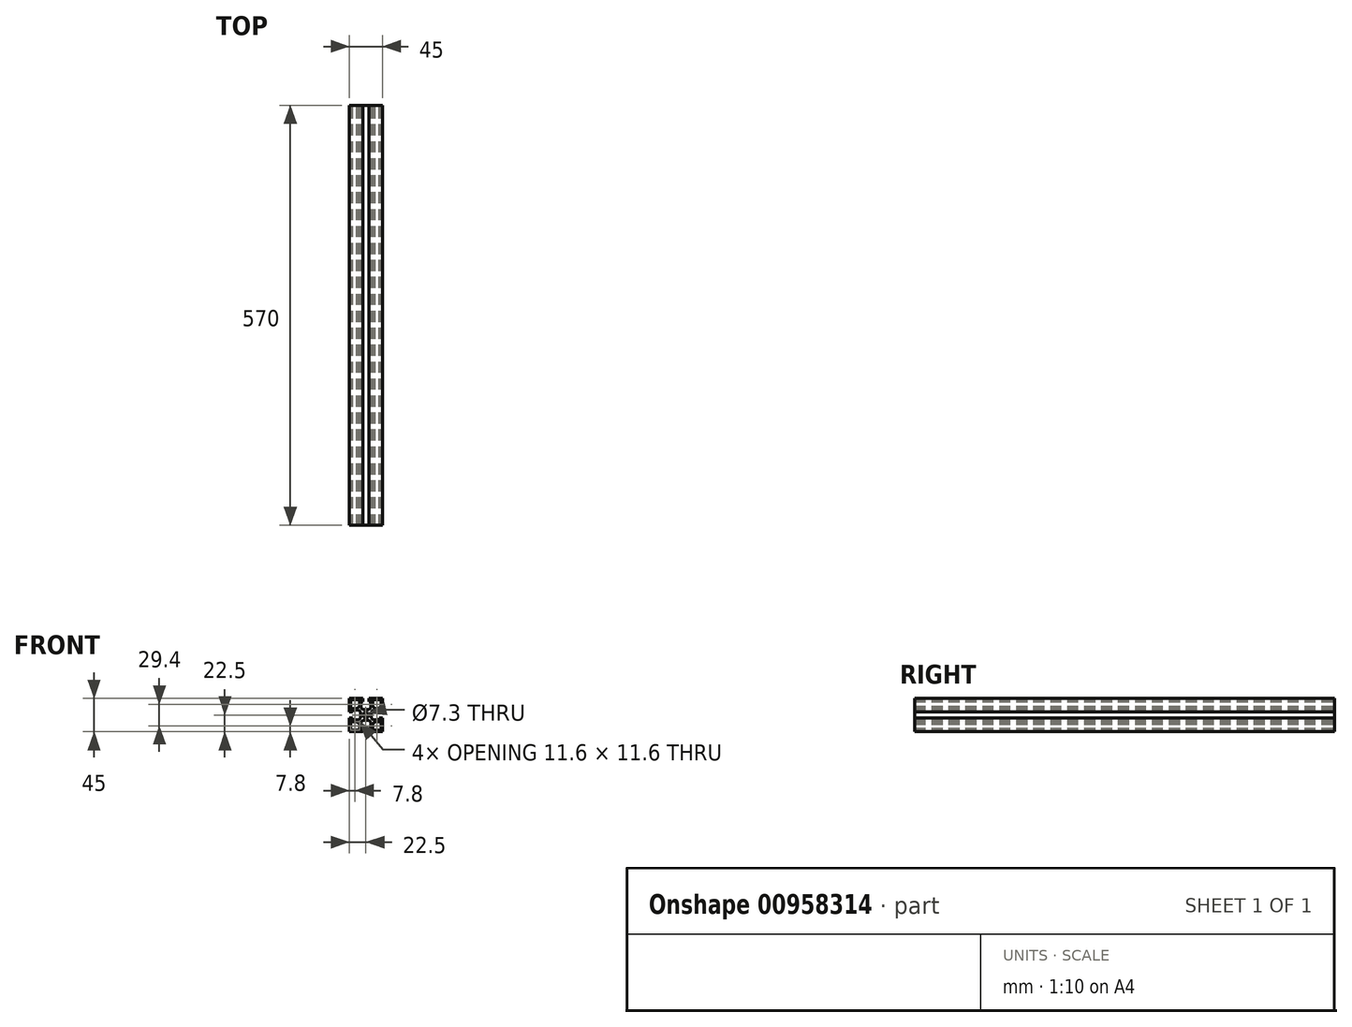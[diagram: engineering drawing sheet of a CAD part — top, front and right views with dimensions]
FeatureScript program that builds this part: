
annotation { "Feature Type Name" : "Feature", "Feature Type Description" : "" }
export const myFeature = defineFeature(function(context is Context, id is Id, definition is map)
    precondition{}
    {
        {
            var Q0;
            Q0=qCreatedBy(makeId("Front.planeOp"),FACE);
            var sketch = newSketch(context, id + "F0", { "sketchPlane" : qUnion([Q0])});
            skLineSegment(sketch, "E0", {"start": v(-22.5, 22.5) * mm, "end": v(-4.15, 22.5) * mm});
            skLineSegment(sketch, "E1", {"start": v(-4.15, 22.5) * mm, "end": v(-4.15, 18) * mm});
            skLineSegment(sketch, "E2", {"start": v(-4.15, 18) * mm, "end": v(-5.75, 18) * mm});
            skArc(sketch, "E3", {"start": v(-5.75, 18) * mm, "mid": v(-6.25, 18.5) * mm, "end": v(-6.75, 18) * mm});
            skLineSegment(sketch, "E4", {"start": v(-6.75, 18) * mm, "end": v(-6.75, 9.8) * mm});
            skLineSegment(sketch, "E5", {"start": v(-6.75, 9.8) * mm, "end": v(-4.15, 7.2) * mm});
            skLineSegment(sketch, "E6", {"start": v(-4.15, 7.2) * mm, "end": v(4.15, 7.2) * mm});
            skLineSegment(sketch, "E7", {"start": v(4.15, 7.2) * mm, "end": v(6.75, 9.8) * mm});
            skLineSegment(sketch, "E8", {"start": v(6.75, 9.8) * mm, "end": v(6.75, 18) * mm});
            skArc(sketch, "E9", {"start": v(6.75, 18) * mm, "mid": v(6.25, 18.5) * mm, "end": v(5.75, 18) * mm});
            skLineSegment(sketch, "E10", {"start": v(5.75, 18) * mm, "end": v(4.15, 18) * mm});
            skLineSegment(sketch, "E11", {"start": v(4.15, 18) * mm, "end": v(4.15, 22.5) * mm});
            skLineSegment(sketch, "E12", {"start": v(4.15, 22.5) * mm, "end": v(22.5, 22.5) * mm});
            skLineSegment(sketch, "E13", {"start": v(22.5, 22.5) * mm, "end": v(22.5, 4.15) * mm});
            skLineSegment(sketch, "E14", {"start": v(22.5, 4.15) * mm, "end": v(18, 4.15) * mm});
            skLineSegment(sketch, "E15", {"start": v(18, 4.15) * mm, "end": v(18, 5.75) * mm});
            skArc(sketch, "E16", {"start": v(18, 5.75) * mm, "mid": v(18.5, 6.25) * mm, "end": v(18, 6.75) * mm});
            skLineSegment(sketch, "E17", {"start": v(18, 6.75) * mm, "end": v(9.8, 6.75) * mm});
            skLineSegment(sketch, "E18", {"start": v(9.8, 6.75) * mm, "end": v(7.2, 4.15) * mm});
            skLineSegment(sketch, "E19", {"start": v(7.2, 4.15) * mm, "end": v(7.2, -4.15) * mm});
            skLineSegment(sketch, "E20", {"start": v(7.2, -4.15) * mm, "end": v(9.8, -6.75) * mm});
            skLineSegment(sketch, "E21", {"start": v(9.8, -6.75) * mm, "end": v(18, -6.75) * mm});
            skArc(sketch, "E22", {"start": v(18, -6.75) * mm, "mid": v(18.5, -6.25) * mm, "end": v(18, -5.75) * mm});
            skLineSegment(sketch, "E23", {"start": v(18, -5.75) * mm, "end": v(18, -4.15) * mm});
            skLineSegment(sketch, "E24", {"start": v(18, -4.15) * mm, "end": v(22.5, -4.15) * mm});
            skLineSegment(sketch, "E25", {"start": v(22.5, -4.15) * mm, "end": v(22.5, -22.5) * mm});
            skLineSegment(sketch, "E26", {"start": v(22.5, -22.5) * mm, "end": v(4.15, -22.5) * mm});
            skLineSegment(sketch, "E27", {"start": v(4.15, -22.5) * mm, "end": v(4.15, -18) * mm});
            skLineSegment(sketch, "E28", {"start": v(4.15, -18) * mm, "end": v(5.75, -18) * mm});
            skArc(sketch, "E29", {"start": v(5.75, -18) * mm, "mid": v(6.25, -18.5) * mm, "end": v(6.75, -18) * mm});
            skLineSegment(sketch, "E30", {"start": v(6.75, -18) * mm, "end": v(6.75, -9.8) * mm});
            skLineSegment(sketch, "E31", {"start": v(6.75, -9.8) * mm, "end": v(4.15, -7.2) * mm});
            skLineSegment(sketch, "E32", {"start": v(4.15, -7.2) * mm, "end": v(-4.15, -7.2) * mm});
            skLineSegment(sketch, "E33", {"start": v(-4.15, -7.2) * mm, "end": v(-6.75, -9.8) * mm});
            skLineSegment(sketch, "E34", {"start": v(-6.75, -9.8) * mm, "end": v(-6.75, -18) * mm});
            skArc(sketch, "E35", {"start": v(-6.75, -18) * mm, "mid": v(-6.25, -18.5) * mm, "end": v(-5.75, -18) * mm});
            skLineSegment(sketch, "E36", {"start": v(-5.75, -18) * mm, "end": v(-4.15, -18) * mm});
            skLineSegment(sketch, "E37", {"start": v(-4.15, -18) * mm, "end": v(-4.15, -22.5) * mm});
            skLineSegment(sketch, "E38", {"start": v(-4.15, -22.5) * mm, "end": v(-22.5, -22.5) * mm});
            skLineSegment(sketch, "E39", {"start": v(-22.5, -22.5) * mm, "end": v(-22.5, -4.15) * mm});
            skLineSegment(sketch, "E40", {"start": v(-22.5, -4.15) * mm, "end": v(-18, -4.15) * mm});
            skLineSegment(sketch, "E41", {"start": v(-18, -4.15) * mm, "end": v(-18, -5.75) * mm});
            skArc(sketch, "E42", {"start": v(-18, -5.75) * mm, "mid": v(-18.5, -6.25) * mm, "end": v(-18, -6.75) * mm});
            skLineSegment(sketch, "E43", {"start": v(-18, -6.75) * mm, "end": v(-9.8, -6.75) * mm});
            skLineSegment(sketch, "E44", {"start": v(-9.8, -6.75) * mm, "end": v(-7.2, -4.15) * mm});
            skLineSegment(sketch, "E45", {"start": v(-7.2, -4.15) * mm, "end": v(-7.2, 4.15) * mm});
            skLineSegment(sketch, "E46", {"start": v(-7.2, 4.15) * mm, "end": v(-9.8, 6.75) * mm});
            skLineSegment(sketch, "E47", {"start": v(-9.8, 6.75) * mm, "end": v(-18, 6.75) * mm});
            skArc(sketch, "E48", {"start": v(-18, 6.75) * mm, "mid": v(-18.5, 6.25) * mm, "end": v(-18, 5.75) * mm});
            skLineSegment(sketch, "E49", {"start": v(-18, 5.75) * mm, "end": v(-18, 4.15) * mm});
            skLineSegment(sketch, "E50", {"start": v(-18, 4.15) * mm, "end": v(-22.5, 4.15) * mm});
            skLineSegment(sketch, "E51", {"start": v(-22.5, 4.15) * mm, "end": v(-22.5, 22.5) * mm});
            skLineSegment(sketch, "E52", {"start": v(-19.5, 20.5) * mm, "end": v(-9.9, 20.5) * mm});
            skArc(sketch, "E53", {"start": v(-8.9, 19.5) * mm, "mid": v(-9.2, 20.2) * mm, "end": v(-9.9, 20.5) * mm});
            skLineSegment(sketch, "E54", {"start": v(-8.9, 19.5) * mm, "end": v(-8.9, 12.1) * mm});
            skLineSegment(sketch, "E55", {"start": v(-8.9, 12.1) * mm, "end": v(-12.1, 8.9) * mm});
            skLineSegment(sketch, "E56", {"start": v(-12.1, 8.9) * mm, "end": v(-19.5, 8.9) * mm});
            skArc(sketch, "E57", {"start": v(-20.5, 9.9) * mm, "mid": v(-20.2, 9.2) * mm, "end": v(-19.5, 8.9) * mm});
            skLineSegment(sketch, "E58", {"start": v(-20.5, 9.9) * mm, "end": v(-20.5, 19.5) * mm});
            skArc(sketch, "E59", {"start": v(-19.5, 20.5) * mm, "mid": v(-20.2, 20.2) * mm, "end": v(-20.5, 19.5) * mm});
            skLineSegment(sketch, "E60", {"start": v(8.9, 12.1) * mm, "end": v(8.9, 19.5) * mm});
            skArc(sketch, "E61", {"start": v(9.9, 20.5) * mm, "mid": v(9.2, 20.2) * mm, "end": v(8.9, 19.5) * mm});
            skLineSegment(sketch, "E62", {"start": v(9.9, 20.5) * mm, "end": v(19.5, 20.5) * mm});
            skArc(sketch, "E63", {"start": v(20.5, 19.5) * mm, "mid": v(20.2, 20.2) * mm, "end": v(19.5, 20.5) * mm});
            skLineSegment(sketch, "E64", {"start": v(20.5, 19.5) * mm, "end": v(20.5, 9.9) * mm});
            skLineSegment(sketch, "E65", {"start": v(19.5, 8.9) * mm, "end": v(12.1, 8.9) * mm});
            skLineSegment(sketch, "E66", {"start": v(12.1, 8.9) * mm, "end": v(8.9, 12.1) * mm});
            skArc(sketch, "E67", {"start": v(19.5, 8.9) * mm, "mid": v(20.2, 9.2) * mm, "end": v(20.5, 9.9) * mm});
            skLineSegment(sketch, "E68", {"start": v(12.1, -8.9) * mm, "end": v(8.9, -12.1) * mm});
            skLineSegment(sketch, "E69", {"start": v(8.9, -12.1) * mm, "end": v(8.9, -19.5) * mm});
            skArc(sketch, "E70", {"start": v(8.9, -19.5) * mm, "mid": v(9.2, -20.2) * mm, "end": v(9.9, -20.5) * mm});
            skLineSegment(sketch, "E71", {"start": v(9.9, -20.5) * mm, "end": v(19.5, -20.5) * mm});
            skLineSegment(sketch, "E72", {"start": v(20.5, -19.5) * mm, "end": v(20.5, -9.9) * mm});
            skArc(sketch, "E73", {"start": v(19.5, -20.5) * mm, "mid": v(20.2, -20.2) * mm, "end": v(20.5, -19.5) * mm});
            skArc(sketch, "E74", {"start": v(20.5, -9.9) * mm, "mid": v(20.2, -9.2) * mm, "end": v(19.5, -8.9) * mm});
            skLineSegment(sketch, "E75", {"start": v(12.1, -8.9) * mm, "end": v(19.5, -8.9) * mm});
            skLineSegment(sketch, "E76", {"start": v(-8.9, -19.5) * mm, "end": v(-8.9, -12.1) * mm});
            skLineSegment(sketch, "E77", {"start": v(-8.9, -12.1) * mm, "end": v(-12.1, -8.9) * mm});
            skLineSegment(sketch, "E78", {"start": v(-12.1, -8.9) * mm, "end": v(-19.5, -8.9) * mm});
            skLineSegment(sketch, "E79", {"start": v(-9.9, -20.5) * mm, "end": v(-19.5, -20.5) * mm});
            skLineSegment(sketch, "E80", {"start": v(-20.5, -19.5) * mm, "end": v(-20.5, -9.9) * mm});
            skArc(sketch, "E81", {"start": v(-19.5, -8.9) * mm, "mid": v(-20.2, -9.2) * mm, "end": v(-20.5, -9.9) * mm});
            skArc(sketch, "E82", {"start": v(-9.9, -20.5) * mm, "mid": v(-9.2, -20.2) * mm, "end": v(-8.9, -19.5) * mm});
            skArc(sketch, "E83", {"start": v(-20.5, -19.5) * mm, "mid": v(-20.2, -20.2) * mm, "end": v(-19.5, -20.5) * mm});
            skCircle(sketch, "E84", {"center": v(0, 0) * mm, "radius": 3.65 * mm});
            skSolve(sketch);
        }
        {
            var Q0;
            Q0=makeQuery(id+"F0.imprint","IMPRINT",FACE,{"disambiguationData":[TD([[makeQuery(id+"F0.imprint","IMPRINT",EDGE,{"derivedFrom":sQuery(id+"F0.wireOp",EDGE,"E0")}),-1.0]])]});
            extrude(context, id + "F1", {"entities" : qUnion([Q0]), "depth" : 570 * mm, "offsetDistance" : 25 * mm});
        }
    });
